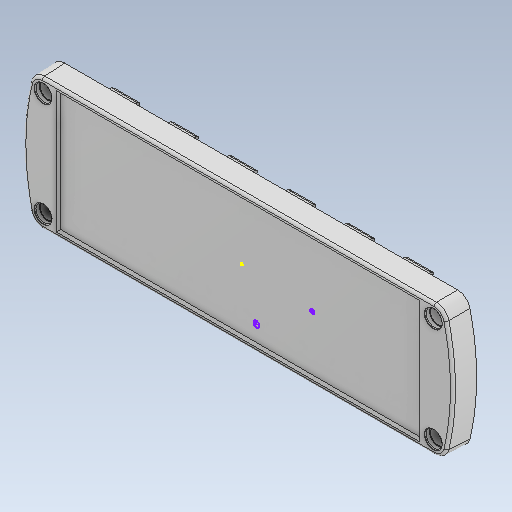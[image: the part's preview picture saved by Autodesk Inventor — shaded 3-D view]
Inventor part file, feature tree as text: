
AUTODESK INVENTOR PART (.ipt)
format: ipt  version: 2021 (Build 250183000, 183)  size: 686,080 bytes
history: native  units: mm
features: other x1, sketch x1
ambient origin geometry x8: Origin, YZ Plane, XZ Plane, XY Plane, X Axis, Y Axis, Z Axis, Center Point
bodies: Solid1 (feature_tree)
feature tree (2):
  other  "1009799_3D"
  sketch  "Sketch1"
